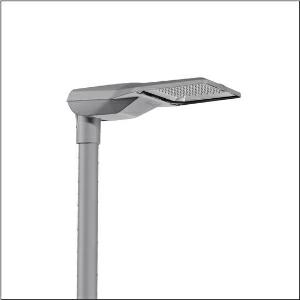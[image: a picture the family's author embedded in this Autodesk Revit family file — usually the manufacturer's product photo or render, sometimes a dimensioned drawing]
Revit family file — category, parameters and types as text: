
# Revit family: streetlight_sl_21_iq_midi___st1_0a_5xe3d31d08nb_3762
name_source: partatom
category: Lighting Fixtures
units: mm (PartAtom-declared; Revit-internal decimal feet)

## family parameters
Cut with Voids When Loaded = No
Host = Face
Light Source = No
Part Type = Normal
Room Calculation Point = No
Round Connector Dimension = Use Diameter
Shared = No

## types (1)
- --- (1 x LED, 23230 lm, 155.5 W, 3000K)
    Apparent Load = 155 VA
    CIE Flux Codes = 40 73 97 100 100
    Color Rendering = 70
    Color Temperature = 3000K
    Default Elevation = 1800 mm
    Description = Streetlight SL 21 iQ midi, mast luminaire, primary light control with lens, of PMMA, primary optical cover: cover, of toughened safety glass, transparent, light distribution: ST1.0a, light emission: direct distribution, primary light characteristic: asymmetric, installation type: post-top, side-entry, LED, High Power LED, rated luminous flux: 23.230lm, luminous efficacy: 149lm/W, light colour: 730, colour temperature: 3000K, control: Auto-Match, Temp-Guard, Lumen-Switch, Night-Set, Smart-Wire, Light-Fading, Desk-Remote (wireless, voltage-free reading and setting of iQ features in the workshop via application-optimized NFC function/RFID function), optimised constant luminous flux control (CLO 2.0), pre-setting: linear dimming characteristic, mains connection: 230..240V, AC, 50/60Hz, start of lifetime: 156W, end of service life: 162W, reduction: 69W, luminaire housing, of diecast aluminium, powder-coated, Siteco® metallic grey (DB 702S), corrosivity category C5 mid according to DIN EN ISO 12944, please order mast flange separately, inclination adjustable: 0°, 5°, 10°, 15°, sealing non-destructively replaceable, multi-level sealing system, length: 644mm, width: 335mm, height: 110mm, mast flange for spigot size: 42mm (side-entry): 5XC10008XM4, 60/48mm (side-entry/post-top): 5XC10108XM2, 76/60mm (side-entry/post-top): 5XC10108XM1, protection rating (complete): IP66, insulation class (complete): insulation class II (safety insulation), certification: CE, ENEC, ENEC+, VDE, impact resistance: IK09, permissible operating ambient temperature for outdoor applications: -40..+50°C, standard-compliant lighting for roads and squares, packaging unit: 1 piece

Light Distribution: ST1.0a
    Height = 111 mm
    Lamp = 1 x LED
    Lamp Light Flux = 23230 lm
    Lamp Power = 155.5 W
    Lamp count = 1
    Length = 644 mm
    Luminous efficacy = 149 lm/W
    Manufacturer = Siteco
    ModVariant = No
    Model = 5XE3D31D08NB
    Number of Poles = 1
    OnlyDefault = Yes
    Power Factor = 1
    Product Name = Streetlight SL 21 iQ midi | ST1.0a
    Product group = mast luminaire | pylon top
    ProductGroupID = 6100
    Protection Class = Protection class II
    Protection Degree = IP 66
    RLX_Detail_Level = 1
    RLX_Emergency_Light_Flux = 0 lm
    RLX_Emergency_Type = 0
    RLX_Emergency_Type_DB = No
    RlxData = <blob elided: 91317 chars, md5=c86312d0>
    Socket = socket
    Standby Power = 0 W
    System Light Flux = 23230 lm
    System Power = 155 W
    Type Comments = factory setting: luminous flux: 100 % | dim-lin: 254 | 823 mA
    Type Image = l_1004298.jpg
    URL = http://relux.com
    VarID = @adj_141657
    Voltage = 0 V
    Weight = 0.00 kg
    Width = 336 mm

## geometry (parser evidence)
native form markers: Blend x4, Sweep x11
no freeform markers — native parametric forms only
